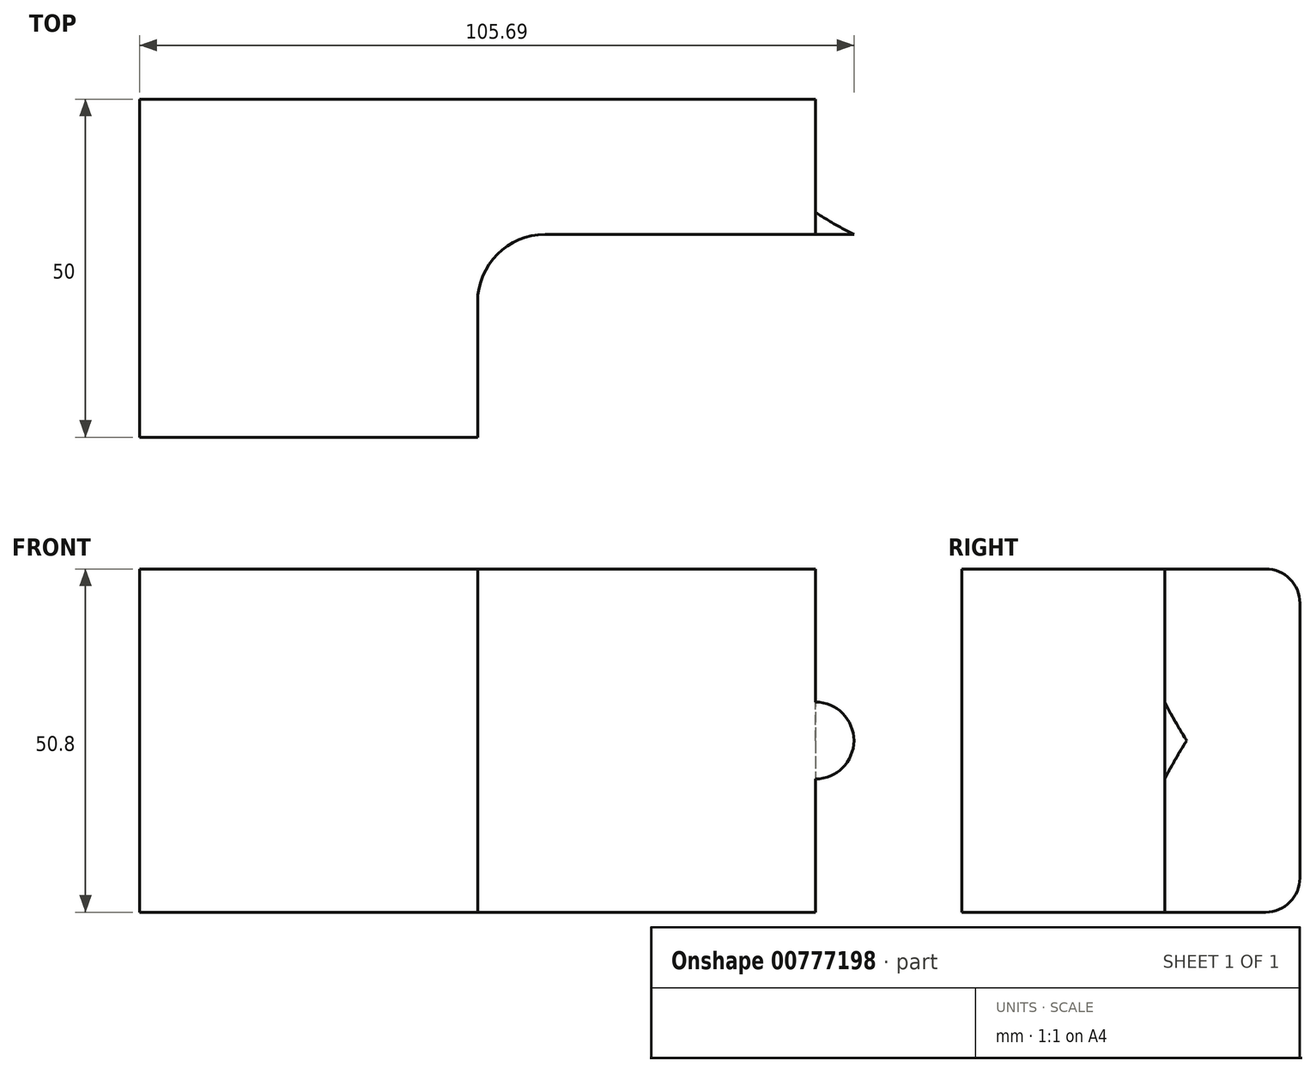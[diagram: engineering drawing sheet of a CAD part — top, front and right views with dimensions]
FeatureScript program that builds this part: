
annotation { "Feature Type Name" : "Feature", "Feature Type Description" : "" }
export const myFeature = defineFeature(function(context is Context, id is Id, definition is map)
    precondition{}
    {
        {
            var Q0;
            Q0=qCreatedBy(makeId("Top.planeOp"),FACE);
            var sketch = newSketch(context, id + "F0", { "sketchPlane" : qUnion([Q0])});
            skLineSegment(sketch, "E0.bottom", {"start": v(-91.25, 47.35) * mm, "end": v(8.75, 47.35) * mm});
            skLineSegment(sketch, "E0.top", {"start": v(-91.25, -2.65) * mm, "end": v(-41.25, -2.65) * mm});
            skLineSegment(sketch, "E0.left", {"start": v(-91.25, 47.35) * mm, "end": v(-91.25, -2.65) * mm});
            skLineSegment(sketch, "E0.right", {"start": v(8.75, 47.35) * mm, "end": v(8.75, 27.35) * mm});
            skLineSegment(sketch, "E1.top", {"start": v(8.75, 27.35) * mm, "end": v(-31.25, 27.35) * mm});
            skLineSegment(sketch, "E1.right", {"start": v(-41.25, -2.65) * mm, "end": v(-41.25, 17.35) * mm});
            skPoint(sketch, "E2.visualSharp", {"position": v(-41.25, 27.35) * mm});
            skArc(sketch, "E2.filletArc", {"start": v(-31.25, 27.35) * mm, "mid": v(-38.32, 24.42) * mm, "end": v(-41.25, 17.35) * mm});
            skFitSpline(sketch, "E3", {"points": [v(8.75, 47.35) * mm, v(56.61, 47.35) * mm, v(78.72, 70.22) * mm, v(60.88, 97.75) * mm, v(16.55, 101.2) * mm], "startDerivative": vector(231.25, -216.53) * mm, "endDerivative": vector(-296.73, 146.9) * mm});
            skLineSegment(sketch, "E4", {"start": v(8.75, 27.35) * mm, "end": v(14.63, 27.35) * mm});
            skFitSpline(sketch, "E5.0", {"points": [v(-0.1, 37.9) * mm, v(2.72, 35.24) * mm, v(6.94, 31.82) * mm, v(12.66, 28.28) * mm, v(17.01, 26.16) * mm, v(21.43, 24.58) * mm, v(25.87, 23.57) * mm, v(30.28, 23.13) * mm, v(34.55, 23.23) * mm, v(38.61, 23.82) * mm, v(42.41, 24.78) * mm, v(45.93, 26.04) * mm, v(49.18, 27.5) * mm, v(52.18, 29.07) * mm, v(54.96, 30.7) * mm, v(57.55, 32.36) * mm, v(59.57, 33.7) * mm, v(61.1, 34.75) * mm, v(62.23, 35.5) * mm, v(63.3, 36.24) * mm, v(64.35, 36.94) * mm, v(65.41, 37.64) * mm, v(66.85, 38.58) * mm, v(68.7, 39.78) * mm, v(70.94, 41.25) * mm, v(73.21, 42.78) * mm, v(75.5, 44.4) * mm, v(78.54, 46.68) * mm, v(81.56, 49.26) * mm, v(84.44, 52.32) * mm, v(86.5, 54.92) * mm, v(88.35, 57.85) * mm, v(89.91, 61.15) * mm, v(90.87, 64.18) * mm, v(91.37, 66.71) * mm, v(91.57, 68.33) * mm, v(91.66, 69.64) * mm, v(91.7, 70.95) * mm, v(91.68, 72.54) * mm, v(91.53, 74.4) * mm, v(91.2, 76.81) * mm, v(90.56, 79.72) * mm, v(89.52, 83.06) * mm, v(88.24, 86.26) * mm, v(86.24, 90.38) * mm, v(83.88, 94.25) * mm, v(81.18, 97.86) * mm, v(78.99, 100.42) * mm, v(76.63, 102.83) * mm, v(74.5, 104.68) * mm, v(72.66, 106.06) * mm, v(71.22, 107.04) * mm, v(69.7, 107.96) * mm, v(68.35, 108.66) * mm, v(67.22, 109.18) * mm, v(66.34, 109.55) * mm, v(65.43, 109.9) * mm, v(64.5, 110.2) * mm, v(63.54, 110.47) * mm, v(62.28, 110.77) * mm, v(60.7, 111.05) * mm, v(58.87, 111.22) * mm, v(56.54, 111.27) * mm, v(53.87, 111.06) * mm, v(51.14, 110.57) * mm, v(48.8, 110.02) * mm, v(46.77, 109.48) * mm, v(44.37, 108.86) * mm, v(42.27, 108.42) * mm, v(40.17, 108.18) * mm, v(38.5, 108.12) * mm, v(36.67, 108.2) * mm, v(34.57, 108.46) * mm, v(32.14, 108.97) * mm, v(28.39, 110.08) * mm, v(24.92, 111.5) * mm, v(22.3, 112.8) * mm]});
            skLineSegment(sketch, "E6", {"start": v(16.55, 101.2) * mm, "end": v(22.3, 112.8) * mm});
            skSolve(sketch);
        }
        {
            var Q0;
            Q0=makeQuery(id+"F0.imprint","IMPRINT",FACE,{"disambiguationData":[TD([[makeQuery(id+"F0.imprint","IMPRINT",EDGE,{"derivedFrom":sQuery(id+"F0.wireOp",EDGE,"E0.bottom")}),-1.0]])]});
            extrude(context, id + "F1", {"entities" : qUnion([Q0]), "depth" : 25.4 * mm, "offsetDistance" : 25.4 * mm, "hasSecondDirection" : true, "secondDirectionOppositeDirection" : true, "secondDirectionDepth" : 25.4 * mm});
        }
        {
            var Q0;
            Q0=makeQuery(id+"F0.imprint","IMPRINT",FACE,{"disambiguationData":[TD([[makeQuery(id+"F0.imprint","IMPRINT",EDGE,{"derivedFrom":sQuery(id+"F0.wireOp",EDGE,"E0.right")}),1.0]])]});
            var Q1;
            Q1=sQuery(id+"F0.wireOp",EDGE,"E0.right");
            revolve(context, id + "F2", {"operationType" : NewBodyOperationType.ADD, "surfaceOperationType" : NewSurfaceOperationType.NEW, "entities" : qUnion([Q0]), "axis" : qUnion([Q1]), "revolveType" : RevolveType.FULL});
        }
        {
            var Q0;
            {var subQ0=sQuery(id+"F0.wireOp",EDGE,"E0.bottom");var subQ1=sQuery(id+"F0.wireOp",EDGE,"E0.left");Q0=makeQuery(id+"F2.boolean.opBoolean","SPLIT",EDGE,{"disambiguationData":[TD([makeQuery(id+"F1.opExtrude","SWEPT_FACE",FACE,{"disambiguationData":[OSD([subQ1])]})])],"derivedFrom":makeQuery(id+"F1.opExtrude","CAP_EDGE",EDGE,{"disambiguationData":[OSD([subQ0])],"isStart":true})});}
            var Q1;
            {var subQ0=sQuery(id+"F0.wireOp",EDGE,"E0.bottom");var subQ1=sQuery(id+"F0.wireOp",EDGE,"E0.left");Q1=makeQuery(id+"F2.boolean.opBoolean","SPLIT",EDGE,{"disambiguationData":[TD([makeQuery(id+"F1.opExtrude","SWEPT_FACE",FACE,{"disambiguationData":[OSD([subQ1])]})])],"derivedFrom":makeQuery(id+"F1.opExtrude","CAP_EDGE",EDGE,{"disambiguationData":[OSD([subQ0])],"isStart":false})});}
            fillet(context, id + "F3", {"entities" : qUnion([Q0, Q1]), "radius" : 5.08 * mm, "tangentPropagation" : true, "allowEdgeOverflow" : false});
        }
    });
